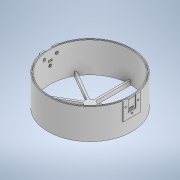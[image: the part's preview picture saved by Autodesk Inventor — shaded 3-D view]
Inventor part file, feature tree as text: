
AUTODESK INVENTOR PART (.ipt)
format: ipt  version: 2020.2 (Build 242310000, 310)  size: 404,992 bytes
history: native  units: mm
features: extrude x8, sketch x8, plane x2, pattern_circular x1
ambient origin geometry x8: Origin, YZ Plane, XZ Plane, XY Plane, X Axis, Y Axis, Z Axis, Center Point
bodies: Solid1 (feature_tree)
feature tree (19):
  extrude  "Extrusion1"  Depth=2.5mm
  extrude  "Extrusion2"  TaperAngle=360.0deg  [1 undecoded]
  plane  "Work Plane2"
  extrude  "Extrusion8"  Depth=215.0mm
  extrude  "Extrusion4"  Depth=67.5mm TaperAngle=0.0deg
  extrude  "Extrusion6"  TaperAngle=0.0deg  [1 undecoded]
  plane  "Work Plane4"
  extrude  "Extrusion9"  Depth=10.0mm
  extrude  "Extrusion10"  Depth=2.0mm
  extrude  "Extrusion11"  Depth=4.0mm TaperAngle=0.0deg
  pattern_circular  "Circular Pattern2"  [2 undecoded]
  sketch  "Sketch2"  dims[d15=2.5mm d34=9.984122mm]
  sketch  "Sketch3"  dims[d35=60.0mm d37=360.0deg]
  sketch  "Sketch5"  dims[d41=10.0mm d42=0.0mm d43=215.0mm]
  sketch  "Sketch7"  dims[d44=205.0mm d45=67.5mm d46=0.0mm]
  sketch  "Sketch9"  dims[d60=20.0mm d61=0.0mm]
  sketch  "Sketch10"  dims[d62=30.0mm d63=10.0mm]
  sketch  "Sketch11"  dims[d64=2.0mm d65=0.0mm d84=208.233333mm]
  sketch  "Sketch12"  dims[d85=211.766667mm d86=4.0mm d87=0.0mm d88=-5.0mm d101=3.0mm d102=0.0mm d103=4.0mm d104=0.0mm d107=2.0mm d108=0.0mm d109=0.0mm d110=45.0mm d111=22.5mm d112=45.0mm d122=3.0mm d123=20.0mm d124=30.0mm d126=5.0mm d127=10.0mm d128=4.0mm d129=4.0mm d130=6.0mm d131=15.0mm d132=4.0mm d133=6.0mm d134=10.0mm d135=15.0mm d136=0.0mm d141=0.0mm d142=20.0mm d143=2.0mm d144=0.0mm d145=6.0mm d146=15.0mm d147=7.0mm d148=7.0mm d149=6.0mm d150=10.0mm d151=0.0mm d152=0.0mm d153=3.0mm d154=5.0mm d155=0.0mm d156=0.0mm d157=20.0mm d158=360.0deg d39=0.5mm d40=0.872665mm]
note: 4 required parameter values undecoded (feature->parameter linkage not recoverable at this tier; creation-order binding heuristic only, values carry confidence <= 0.55)
